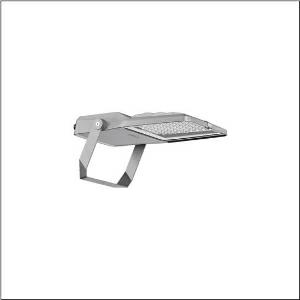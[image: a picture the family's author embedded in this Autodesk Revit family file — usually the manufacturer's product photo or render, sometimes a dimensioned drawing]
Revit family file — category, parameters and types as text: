
# Revit family: floodlight_fl_21_iq_mini___pl52_5xa7771b2d1a_9873
name_source: partatom
category: Lighting Fixtures
units: mm (PartAtom-declared; Revit-internal decimal feet)

## family parameters
Cut with Voids When Loaded = No
Host = Face
Light Source = No
Part Type = Normal
Room Calculation Point = No
Round Connector Dimension = Use Diameter
Shared = No

## types (1)
- --- (1 x LED, 6240 lm, 45.5 W, 3000K)
    Apparent Load = 46 VA
    CIE Flux Codes = 26 60 98 100 100
    Color Rendering = 70
    Color Temperature = 3000K
    Default Elevation = 1800 mm
    Description = Floodlight FL 21 iQ mini, floodlight, primary light control with lens, of PMMA, primary optical cover: protective disc, of toughened safety glass, transparent, light distribution: PL52, light emission: direct distribution, installation type: surface-mounted, lamps: LED, High Power LED, rated values: 6.240lm | 45,5W | 137,1lm/W (begin service life); end service life: 6.240lm | 48W; at 50% lumin. flux: 3.120lm | 21,5W | 145,1lm/W, colour temperature: 3000K, colour rendering: CRI > 70, light colour: 730, light setting 1 begin service life: 100% | 6.240lm | 45,5W | 137,1lm/W | 3.000K, light setting 1 end service life: 48W, further light settings possible, control: Auto-Match, Temp-Guard, Lumen-Switch, Night-Set, Smart-Wire, Light-Fading, Desk-Remote (wireless, voltage-free reading and setting of iQ features in the workshop via application-optimized NFC function/RFID function), optimised constant luminous flux control (CLO 2.0), pre-setting: linear dimming characteristic, with terminal, 6-pole, mains connection: 220..240V, AC, 50/60Hz, luminaire housing, of diecast aluminium, powder-coated, SITECO metallic grey (DB 702S), corrosivity category C5 mid according to DIN EN ISO 12944suitable for swimming poolschlorine-resistant, sealing non-destructively replaceable, mounting bracket, of steel, galvanised, powder-coated, SITECO metallic grey (DB 702S), protection rating (complete): IP66, insulation class (complete): insulation class II (safety insulation), certification: CE, ENEC, VDE, protection symbol: D, impact resistance: IK08, permissible operating ambient temperature: -40..+40°C, permissible operating ambient temperature for outdoor applications: -40..+50°C, standard: DIN EN 12944, LABS conformity tested according to VDMA 24364:2018-05, packaging unit: 1 piece

Light Distribution: PL52
    Height = 70 mm
    Lamp = 1 x LED
    Lamp Light Flux = 6240 lm
    Lamp Power = 45.5 W
    Lamp count = 1
    Length = 485 mm
    Luminous efficacy = 137 lm/W
    Manufacturer = Siteco
    ModVariant = No
    Model = 5XA7771B2D1A
    Mounting Place = Wall
    Mounting Type = Surface mounted
    Number of Poles = 1
    OnlyDefault = Yes
    Power Factor = 1
    Product Name = Floodlight FL 21 iQ mini | PL52
    Product group = floodlight | wall mounted
    ProductGroupID = 2002
    Protection Class = Protection class II
    Protection Degree = IP 66
    RLX_Detail_Level = 1
    RLX_Emergency_Light_Flux = 0 lm
    RLX_Emergency_Type = 0
    RLX_Emergency_Type_DB = No
    RlxData = <blob elided: 96553 chars, md5=1e8af376>
    Socket = socket
    Standby Power = 0 W
    System Light Flux = 6240 lm
    System Power = 46 W
    Type Comments = factory setting: luminous flux: 100 % | dim-lin: 254 | 463 mA
    Type Image = l_1006845.jpg
    URL = http://relux.com
    VarID = @adj_164637
    Voltage = 0 V
    Weight = 0.00 kg
    Width = 337 mm

## geometry (parser evidence)
native form markers: Blend x4, Sweep x13
no freeform markers — native parametric forms only
